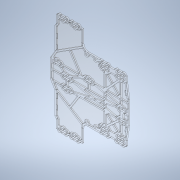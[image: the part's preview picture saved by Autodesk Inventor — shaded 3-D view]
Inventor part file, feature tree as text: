
AUTODESK INVENTOR PART (.ipt)
format: ipt  version: 2020.2 (Build 242310000, 310)  size: 10,906,624 bytes
history: native  units: mm
features: sketch x39, extrude x37, projected_geometry x21, other x15, fillet x10, hole x2
ambient origin geometry x8: Origin, YZ Plane, XZ Plane, XY Plane, X Axis, Y Axis, Z Axis, Center Point
bodies: Body1 (feature_tree)
feature tree (124):
  other  "ソリッド1"
  extrude  "押し出し1"  Depth=2.0mm
  fillet  "フィレット1"  Radius=2.0mm
  fillet  "フィレット2"  Radius=2.0mm
  fillet  "フィレット3"  Radius=2.0mm
  extrude  "押し出し2"  Depth=2.0mm
  extrude  "押し出し3"  Depth=2.0mm
  sketch  "スケッチ4"
  extrude  "押し出し4"  Depth=2.0mm
  extrude  "押し出し5"  Depth=2.0mm
  extrude  "押し出し6"  Depth=2.0mm
  sketch  "スケッチ6"
  extrude  "押し出し7"  Depth=2.0mm
  extrude  "押し出し8"  Depth=2.0mm
  extrude  "押し出し9"  Depth=2.0mm
  extrude  "押し出し10"  Depth=2.0mm
  sketch  "スケッチ8"
  extrude  "押し出し11"  Depth=2.0mm
  extrude  "押し出し12"  Depth=2.0mm
  fillet  "フィレット4"  Radius=2.0mm
  sketch  "スケッチ9"
  sketch  "スケッチ10"
  extrude  "押し出し13"  Depth=2.0mm
  extrude  "押し出し14"  Depth=2.0mm
  hole  "穴1"  [1 undecoded]
  sketch  "スケッチ12"
  extrude  "押し出し15"  Depth=2.0mm
  extrude  "押し出し16"  Depth=2.0mm
  fillet  "フィレット5"  Radius=2.0mm
  sketch  "スケッチ13"
  sketch  "スケッチ15"
  sketch  "スケッチ16"
  sketch  "スケッチ17"
  sketch  "スケッチ18"
  extrude  "押し出し20"  Depth=2.0mm
  extrude  "押し出し21"  Depth=2.0mm
  sketch  "スケッチ19"
  extrude  "押し出し22"  Depth=3.0mm
  extrude  "押し出し23"  Depth=3.0mm
  fillet  "フィレット6"  Radius=3.0mm
  extrude  "押し出し24"  Depth=3.0mm
  hole  "穴2"  [1 undecoded]
  sketch  "スケッチ24"
  fillet  "フィレット7"  Radius=3.0mm
  extrude  "押し出し25"  Depth=4.828426mm
  extrude  "押し出し26"  Depth=5.0mm
  extrude  "押し出し27"  Depth=9.0mm
  fillet  "フィレット8"  Radius=9.0mm
  extrude  "押し出し28"  Depth=9.0mm
  sketch  "スケッチ29"
  sketch  "スケッチ30"
  extrude  "押し出し29"  Depth=9.0mm
  extrude  "押し出し30"  Depth=9.0mm
  sketch  "スケッチ32"
  extrude  "押し出し31"  Depth=9.0mm
  extrude  "押し出し32"  Depth=9.0mm
  extrude  "押し出し33"  Depth=9.0mm
  fillet  "フィレット9"  Radius=2.0mm
  extrude  "押し出し34"  Depth=2.0mm
  fillet  "フィレット10"  Radius=2.0mm
  extrude  "押し出し35"  Depth=2.0mm
  sketch  "スケッチ36"
  sketch  "スケッチ37"
  sketch  "スケッチ38"
  extrude  "押し出し36"  Depth=2.0mm
  extrude  "押し出し37"  Depth=2.0mm
  extrude  "押し出し38"  Depth=2.0mm
  extrude  "押し出し39"  Depth=2.0mm
  extrude  "押し出し40"  Depth=3.0mm
  sketch  "スケッチ1"
  sketch  "スケッチ2"
  sketch  "スケッチ3"
  sketch  "スケッチ5"
  projected_geometry  "投影ループ1"
  projected_geometry  "投影ループ2"
  sketch  "スケッチ7"
  projected_geometry  "投影ループ3"
  projected_geometry  "投影ループ4"
  sketch  "スケッチ11"
  projected_geometry  "投影ループ5"
  projected_geometry  "投影ループ6"
  projected_geometry  "投影ループ7"
  projected_geometry  "投影ループ9"
  projected_geometry  "投影ループ10"
  sketch  "スケッチ20"
  projected_geometry  "投影ループ11"
  sketch  "スケッチ21"
  projected_geometry  "投影ループ12"
  sketch  "スケッチ22"
  projected_geometry  "投影ループ13"
  sketch  "スケッチ23"
  projected_geometry  "投影ループ14"
  projected_geometry  "投影ループ15"
  sketch  "スケッチ25"
  projected_geometry  "投影ループ16"
  sketch  "スケッチ26"
  sketch  "スケッチ27"
  sketch  "スケッチ28"
  projected_geometry  "投影ループ17"
  projected_geometry  "投影ループ18"
  sketch  "スケッチ31"
  projected_geometry  "投影ループ19"
  projected_geometry  "投影ループ20"
  sketch  "スケッチ33"
  projected_geometry  "投影ループ21"
  sketch  "スケッチ34"
  projected_geometry  "投影ループ22"
  sketch  "スケッチ35"
  sketch  "スケッチ39"
  sketch  "スケッチ40"
  other  "断面エッジを投影1"
  other  "断面エッジを投影2"
  other  "断面エッジを投影3"
  other  "断面エッジを投影4"
  other  "断面エッジを投影5"
  other  "断面エッジを投影6"
  other  "断面エッジを投影7"
  other  "断面エッジを投影8"
  other  "断面エッジを投影9"
  other  "断面エッジを投影10"
  other  "断面エッジを投影11"
  other  "断面エッジを投影12"
  other  "断面エッジを投影13"
  other  "断面エッジを投影14"
note: 2 required parameter values undecoded (feature->parameter linkage not recoverable at this tier; creation-order binding heuristic only, values carry confidence <= 0.55)
